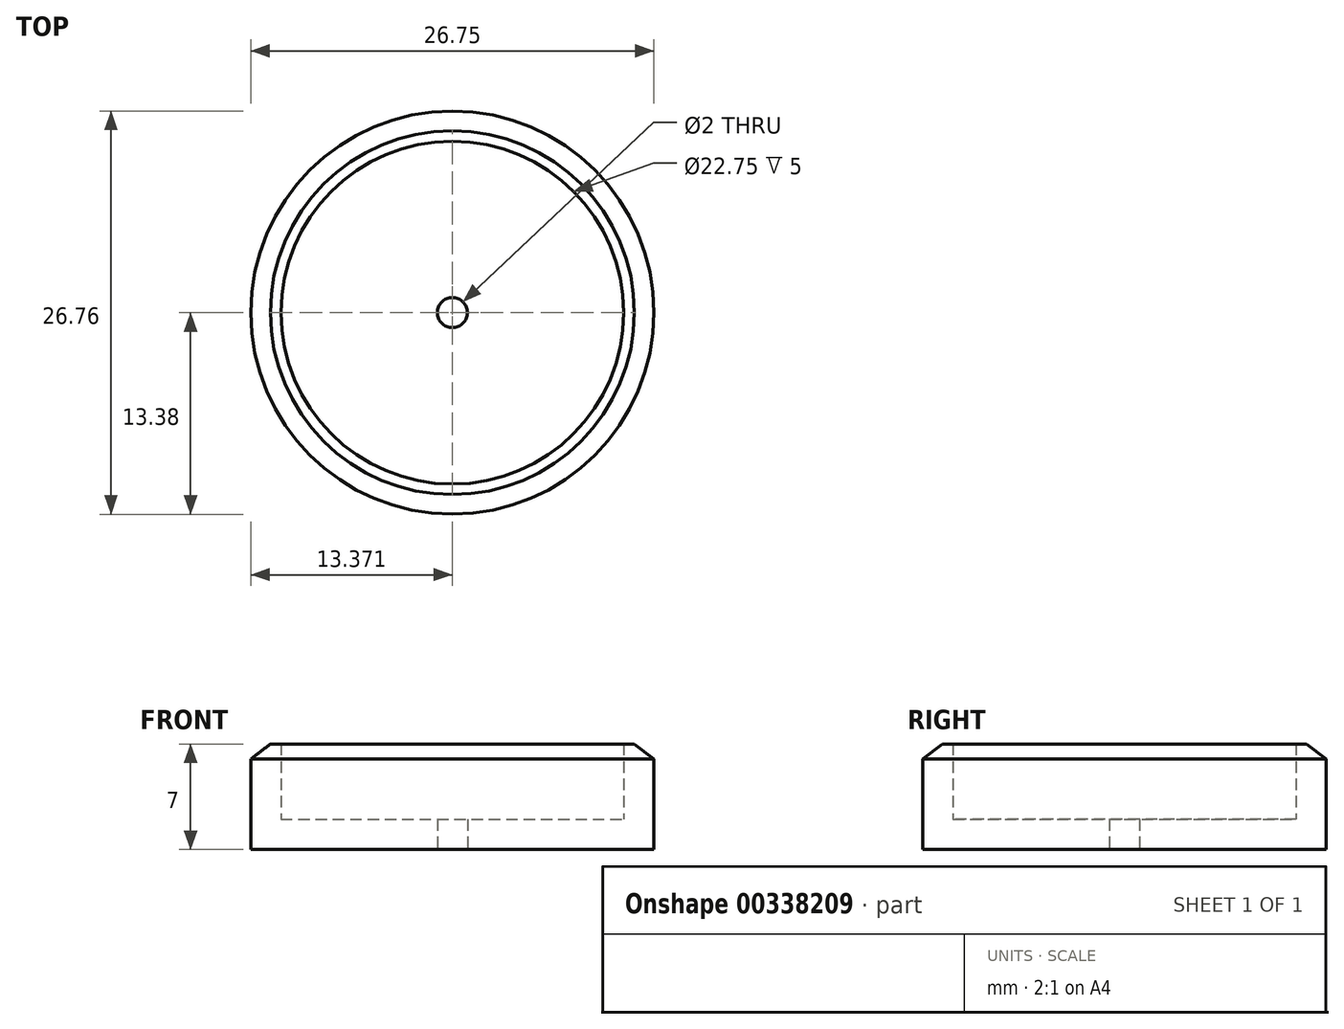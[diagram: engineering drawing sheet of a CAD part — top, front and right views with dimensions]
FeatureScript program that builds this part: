
annotation { "Feature Type Name" : "Feature", "Feature Type Description" : "" }
export const myFeature = defineFeature(function(context is Context, id is Id, definition is map)
    precondition{}
    {
        {
            var Q0;
            Q0=qCreatedBy(makeId("Front.planeOp"),FACE);
            var sketch = newSketch(context, id + "F0", { "sketchPlane" : qUnion([Q0])});
            skLineSegment(sketch, "E0", {"start": v(6.58, -6.35) * mm, "end": v(6.58, -4.35) * mm, "construction": true});
            skLineSegment(sketch, "E1", {"start": v(6.58, -6.35) * mm, "end": v(5.58, -6.35) * mm, "construction": true});
            skLineSegment(sketch, "E2", {"start": v(5.58, -6.35) * mm, "end": v(5.58, -4.35) * mm, "construction": true});
            skLineSegment(sketch, "E3", {"start": v(5.58, -4.35) * mm, "end": v(6.58, -4.35) * mm, "construction": true});
            skLineSegment(sketch, "E4", {"start": v(5.58, -6.35) * mm, "end": v(-6.8, -6.35) * mm});
            skLineSegment(sketch, "E5", {"start": v(5.58, -4.35) * mm, "end": v(-4.8, -4.35) * mm});
            skLineSegment(sketch, "E6", {"start": v(-6.8, -0.35) * mm, "end": v(-6.8, -6.35) * mm});
            skLineSegment(sketch, "E7", {"start": v(-6.8, -0.35) * mm, "end": v(-5.5, 0.65) * mm});
            skLineSegment(sketch, "E8", {"start": v(-5.5, 0.65) * mm, "end": v(-4.8, 0.65) * mm});
            skLineSegment(sketch, "E9", {"start": v(5.58, -4.35) * mm, "end": v(5.58, -6.35) * mm});
            skPoint(sketch, "E10.end.orphan", {"position": v(-4.8, -0.35) * mm});
            skLineSegment(sketch, "E11", {"start": v(-4.8, -4.35) * mm, "end": v(-4.8, 0.65) * mm});
            skSolve(sketch);
        }
        {
            var Q0;
            Q0 = qSketchRegion(id + "F0", true);
            var Q1;
            Q1=sQuery(id+"F0.wireOp",EDGE,"E0");
            revolve(context, id + "F1", {"entities" : qUnion([Q0]), "axis" : qUnion([Q1]), "revolveType" : RevolveType.FULL});
        }
    });
